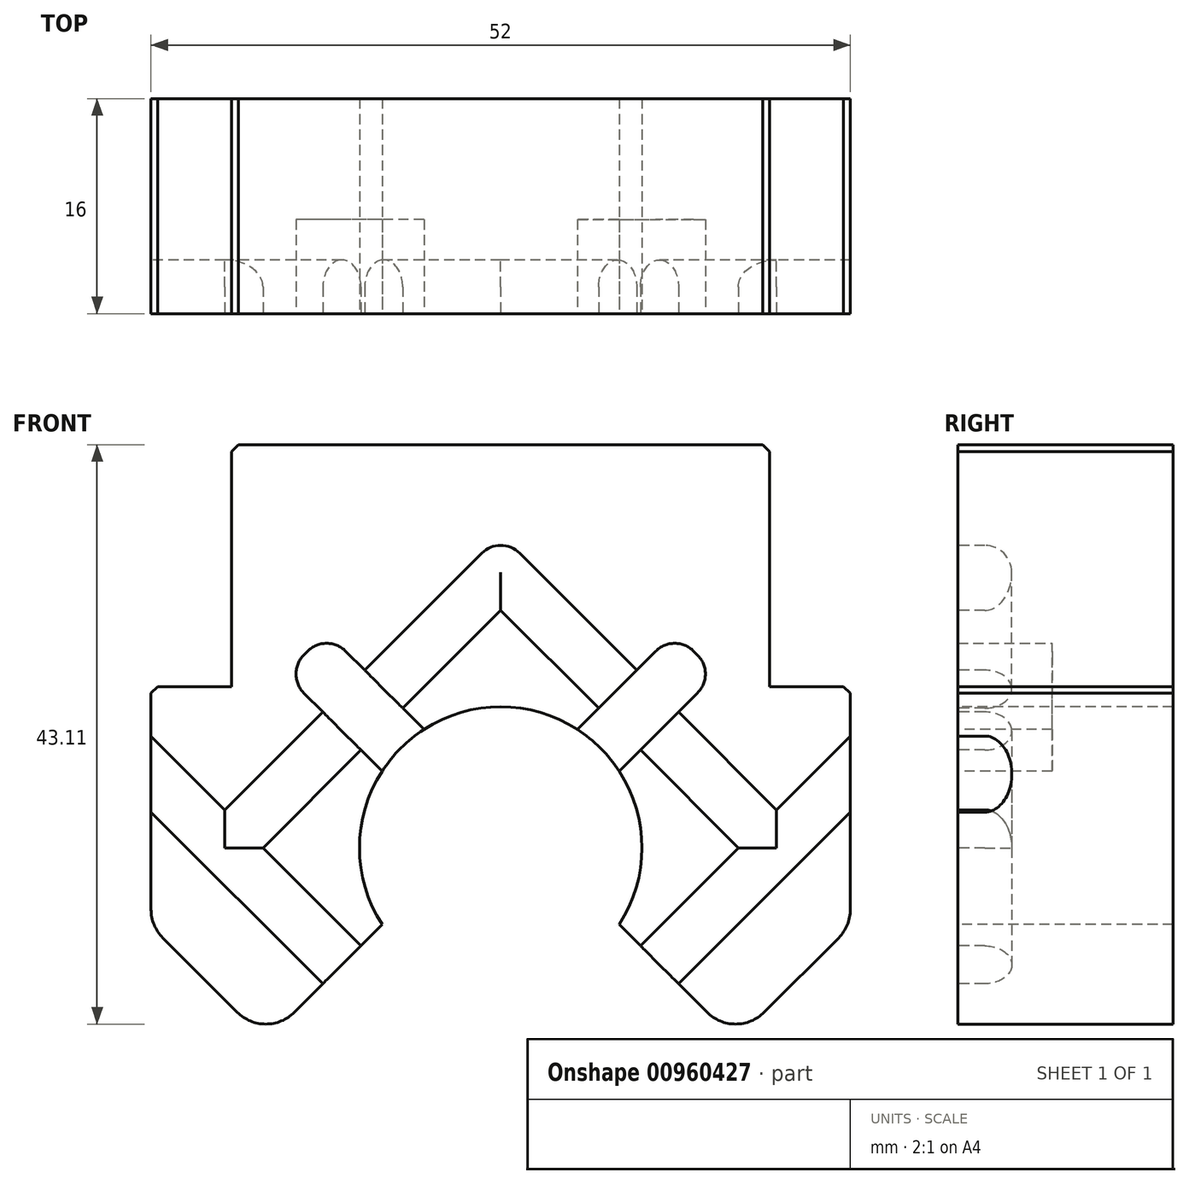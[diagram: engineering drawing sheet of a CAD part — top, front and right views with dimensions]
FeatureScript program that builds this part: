
annotation { "Feature Type Name" : "Feature", "Feature Type Description" : "" }
export const myFeature = defineFeature(function(context is Context, id is Id, definition is map)
    precondition{}
    {
        {
            var Q0;
            Q0=qCreatedBy(makeId("Front.planeOp"),FACE);
            var sketch = newSketch(context, id + "F0", { "sketchPlane" : qUnion([Q0])});
            skLineSegment(sketch, "E0", {"start": v(-23.46, -23.46) * mm, "end": v(26.19, 26.19) * mm, "construction": true});
            skLineSegment(sketch, "E1", {"start": v(-0.37, 20.88) * mm, "end": v(20.54, -0.03) * mm, "construction": true});
            skArc(sketch, "E2", {"start": v(8.82, -5.7) * mm, "mid": v(0, 10.5) * mm, "end": v(-8.82, -5.7) * mm});
            skLineSegment(sketch, "E3", {"start": v(0, -23.09) * mm, "end": v(0, 36.36) * mm, "construction": true});
            skLineSegment(sketch, "E4", {"start": v(-33.15, 0) * mm, "end": v(34.43, 0) * mm, "construction": true});
            skLineSegment(sketch, "E5", {"start": v(0, 30) * mm, "end": v(20, 30) * mm});
            skLineSegment(sketch, "E6", {"start": v(20, 30) * mm, "end": v(20, 12) * mm});
            skLineSegment(sketch, "E7", {"start": v(20, 12) * mm, "end": v(26, 12) * mm});
            skLineSegment(sketch, "E8", {"start": v(26, 12) * mm, "end": v(26, -5.82) * mm});
            skLineSegment(sketch, "E9.MirrorCS", {"start": v(0, 30) * mm, "end": v(-20, 30) * mm});
            skLineSegment(sketch, "E10.MirrorCS", {"start": v(-20, 30) * mm, "end": v(-20, 12) * mm});
            skLineSegment(sketch, "E11.MirrorCS", {"start": v(-20, 12) * mm, "end": v(-26, 12) * mm});
            skLineSegment(sketch, "E12.MirrorCS", {"start": v(-26, 12) * mm, "end": v(-26, -5.82) * mm});
            skLineSegment(sketch, "E13", {"start": v(5.7, 8.82) * mm, "end": v(12.94, 16.05) * mm});
            skLineSegment(sketch, "E14.MirrorCS", {"start": v(8.82, 5.7) * mm, "end": v(16.05, 12.94) * mm});
            skLineSegment(sketch, "E15", {"start": v(12.94, 16.05) * mm, "end": v(16.05, 12.94) * mm});
            skLineSegment(sketch, "E16", {"start": v(0, 17.68) * mm, "end": v(17.68, 0) * mm});
            skLineSegment(sketch, "E17", {"start": v(0, 23.33) * mm, "end": v(20.5, 2.83) * mm});
            skLineSegment(sketch, "E18.MirrorCS", {"start": v(-5.7, 8.82) * mm, "end": v(-12.94, 16.05) * mm});
            skLineSegment(sketch, "E19.MirrorCS", {"start": v(-8.82, 5.7) * mm, "end": v(-16.05, 12.94) * mm});
            skLineSegment(sketch, "E20.MirrorCS", {"start": v(-12.94, 16.05) * mm, "end": v(-16.05, 12.94) * mm});
            skLineSegment(sketch, "E21.MirrorCS", {"start": v(13.22, -10.11) * mm, "end": v(26, 2.67) * mm});
            skLineSegment(sketch, "E22.MirrorCS", {"start": v(10.4, -7.28) * mm, "end": v(17.68, 0) * mm});
            skLineSegment(sketch, "E23.trimOffspring", {"start": v(20.5, 2.83) * mm, "end": v(26, 8.32) * mm});
            skLineSegment(sketch, "E24.MirrorCS", {"start": v(-13.22, -10.11) * mm, "end": v(-26, 2.67) * mm});
            skLineSegment(sketch, "E25.MirrorCS", {"start": v(-10.4, -7.28) * mm, "end": v(-17.68, 0) * mm});
            skLineSegment(sketch, "E26.MirrorCS", {"start": v(0, 17.68) * mm, "end": v(-17.68, 0) * mm});
            skLineSegment(sketch, "E27.MirrorCS", {"start": v(0, 23.33) * mm, "end": v(-20.5, 2.83) * mm});
            skLineSegment(sketch, "E28.MirrorCS", {"start": v(-20.5, 2.83) * mm, "end": v(-26, 8.32) * mm});
            skLineSegment(sketch, "E29", {"start": v(8.82, -5.7) * mm, "end": v(17.47, -14.35) * mm});
            skLineSegment(sketch, "E30", {"start": v(17.47, -14.35) * mm, "end": v(26, -5.82) * mm});
            skLineSegment(sketch, "E31.MirrorCS", {"start": v(-17.47, -14.35) * mm, "end": v(-26, -5.82) * mm});
            skLineSegment(sketch, "E32.MirrorCS", {"start": v(-8.82, -5.7) * mm, "end": v(-17.47, -14.35) * mm});
            skSolve(sketch);
        }
        {
            var Q0;
            {var subQ1=sQuery(id+"F0.wireOp",EDGE,"E2");var subQ7=sQuery(id+"F0.wireOp",EDGE,"E13");var subQ9=makeQuery(id+"F0.imprint","INTERSECT",VERTEX,{"derivedFrom":[subQ1,subQ7]});Q0=makeQuery(id+"F0.imprint","IMPRINT",FACE,{"disambiguationData":[TD([[makeQuery(id+"F0.imprint","IMPRINT",EDGE,{"disambiguationData":[TD([[subQ9,-1.0]])],"derivedFrom":subQ1}),-1.0]])]});}
            var Q1;
            {var subQ0=sQuery(id+"F0.wireOp",EDGE,"E18.MirrorCS");var subQ1=sQuery(id+"F0.wireOp",EDGE,"E2");var subQ2=makeQuery(id+"F0.imprint","INTERSECT",VERTEX,{"derivedFrom":[subQ1,subQ0]});Q1=makeQuery(id+"F0.imprint","IMPRINT",FACE,{"disambiguationData":[TD([[makeQuery(id+"F0.imprint","IMPRINT",EDGE,{"disambiguationData":[TD([[subQ2,-1.0]])],"derivedFrom":subQ1}),-1.0]])]});}
            var Q2;
            {var subQ3=sQuery(id+"F0.wireOp",EDGE,"E25.MirrorCS");Q2=makeQuery(id+"F0.imprint","IMPRINT",FACE,{"disambiguationData":[TD([[makeQuery(id+"F0.imprint","IMPRINT",EDGE,{"derivedFrom":subQ3}),-1.0]])]});}
            var Q3;
            {var subQ0=sQuery(id+"F0.wireOp",EDGE,"E13");var subQ1=sQuery(id+"F0.wireOp",EDGE,"E2");var subQ2=makeQuery(id+"F0.imprint","INTERSECT",VERTEX,{"derivedFrom":[subQ1,subQ0]});Q3=makeQuery(id+"F0.imprint","IMPRINT",FACE,{"disambiguationData":[TD([[makeQuery(id+"F0.imprint","IMPRINT",EDGE,{"disambiguationData":[TD([[subQ2,1.0]])],"derivedFrom":subQ1}),-1.0]])]});}
            var Q4;
            {var subQ7=sQuery(id+"F0.wireOp",EDGE,"E13");var subQ9=sQuery(id+"F0.wireOp",EDGE,"E16");var subQ11=makeQuery(id+"F0.imprint","INTERSECT",VERTEX,{"derivedFrom":[subQ7,subQ9]});Q4=makeQuery(id+"F0.imprint","IMPRINT",FACE,{"disambiguationData":[TD([[makeQuery(id+"F0.imprint","IMPRINT",EDGE,{"disambiguationData":[TD([[subQ11,-1.0]])],"derivedFrom":subQ7}),1.0]])]});}
            var Q5;
            {var subQ0=sQuery(id+"F0.wireOp",EDGE,"E16");var subQ1=sQuery(id+"F0.wireOp",EDGE,"E13");var subQ2=makeQuery(id+"F0.imprint","INTERSECT",VERTEX,{"derivedFrom":[subQ1,subQ0]});Q5=makeQuery(id+"F0.imprint","IMPRINT",FACE,{"disambiguationData":[TD([[makeQuery(id+"F0.imprint","IMPRINT",EDGE,{"disambiguationData":[TD([[subQ2,-1.0]])],"derivedFrom":subQ1}),-1.0]])]});}
            var Q6;
            {var subQ0=sQuery(id+"F0.wireOp",EDGE,"E26.MirrorCS");var subQ1=sQuery(id+"F0.wireOp",EDGE,"E18.MirrorCS");var subQ2=makeQuery(id+"F0.imprint","INTERSECT",VERTEX,{"derivedFrom":[subQ1,subQ0]});Q6=makeQuery(id+"F0.imprint","IMPRINT",FACE,{"disambiguationData":[TD([[makeQuery(id+"F0.imprint","IMPRINT",EDGE,{"disambiguationData":[TD([[subQ2,-1.0]])],"derivedFrom":subQ1}),1.0]])]});}
            var Q7;
            {var subQ0=sQuery(id+"F0.wireOp",EDGE,"E24.MirrorCS");Q7=makeQuery(id+"F0.imprint","IMPRINT",FACE,{"disambiguationData":[TD([[makeQuery(id+"F0.imprint","IMPRINT",EDGE,{"derivedFrom":subQ0}),-1.0]])]});}
            var Q8;
            {var subQ0=sQuery(id+"F0.wireOp",EDGE,"E20.MirrorCS");Q8=makeQuery(id+"F0.imprint","IMPRINT",FACE,{"disambiguationData":[TD([[makeQuery(id+"F0.imprint","IMPRINT",EDGE,{"derivedFrom":subQ0}),1.0]])]});}
            var Q9;
            {var subQ0=sQuery(id+"F0.wireOp",EDGE,"E21.MirrorCS");Q9=makeQuery(id+"F0.imprint","IMPRINT",FACE,{"disambiguationData":[TD([[makeQuery(id+"F0.imprint","IMPRINT",EDGE,{"derivedFrom":subQ0}),1.0]])]});}
            var Q10;
            {var subQ0=sQuery(id+"F0.wireOp",EDGE,"E22.MirrorCS");Q10=makeQuery(id+"F0.imprint","IMPRINT",FACE,{"disambiguationData":[TD([[makeQuery(id+"F0.imprint","IMPRINT",EDGE,{"derivedFrom":subQ0}),1.0]])]});}
            var Q11;
            Q11=makeQuery(id+"F0.imprint","IMPRINT",FACE,{"disambiguationData":[TD([[makeQuery(id+"F0.imprint","IMPRINT",EDGE,{"derivedFrom":sQuery(id+"F0.wireOp",EDGE,"E5")}),-1.0]])]});
            var Q12;
            {var subQ0=sQuery(id+"F0.wireOp",EDGE,"E15");Q12=makeQuery(id+"F0.imprint","IMPRINT",FACE,{"disambiguationData":[TD([[makeQuery(id+"F0.imprint","IMPRINT",EDGE,{"derivedFrom":subQ0}),-1.0]])]});}
            var Q13;
            {var subQ2=sQuery(id+"F0.wireOp",EDGE,"E21.MirrorCS");Q13=makeQuery(id+"F0.imprint","IMPRINT",FACE,{"disambiguationData":[TD([[makeQuery(id+"F0.imprint","IMPRINT",EDGE,{"derivedFrom":subQ2}),-1.0]])]});}
            var Q14;
            {var subQ2=sQuery(id+"F0.wireOp",EDGE,"E24.MirrorCS");Q14=makeQuery(id+"F0.imprint","IMPRINT",FACE,{"disambiguationData":[TD([[makeQuery(id+"F0.imprint","IMPRINT",EDGE,{"derivedFrom":subQ2}),1.0]])]});}
            extrude(context, id + "F1", {"entities" : qUnion([Q0, Q1, Q2, Q3, Q4, Q5, Q6, Q7, Q8, Q9, Q10, Q11, Q12, Q13, Q14]), "oppositeDirection" : true, "depth" : 16 * mm, "offsetDistance" : 25 * mm});
        }
        {
            var Q0;
            {var subQ0=sQuery(id+"F0.wireOp",EDGE,"E15");Q0=makeQuery(id+"F0.imprint","IMPRINT",FACE,{"disambiguationData":[TD([[makeQuery(id+"F0.imprint","IMPRINT",EDGE,{"derivedFrom":subQ0}),-1.0]])]});}
            var Q1;
            {var subQ0=sQuery(id+"F0.wireOp",EDGE,"E16");var subQ1=sQuery(id+"F0.wireOp",EDGE,"E13");var subQ2=makeQuery(id+"F0.imprint","INTERSECT",VERTEX,{"derivedFrom":[subQ1,subQ0]});Q1=makeQuery(id+"F0.imprint","IMPRINT",FACE,{"disambiguationData":[TD([[makeQuery(id+"F0.imprint","IMPRINT",EDGE,{"disambiguationData":[TD([[subQ2,-1.0]])],"derivedFrom":subQ1}),-1.0]])]});}
            var Q2;
            {var subQ0=sQuery(id+"F0.wireOp",EDGE,"E13");var subQ1=sQuery(id+"F0.wireOp",EDGE,"E2");var subQ2=makeQuery(id+"F0.imprint","INTERSECT",VERTEX,{"derivedFrom":[subQ1,subQ0]});Q2=makeQuery(id+"F0.imprint","IMPRINT",FACE,{"disambiguationData":[TD([[makeQuery(id+"F0.imprint","IMPRINT",EDGE,{"disambiguationData":[TD([[subQ2,1.0]])],"derivedFrom":subQ1}),-1.0]])]});}
            var Q3;
            {var subQ0=sQuery(id+"F0.wireOp",EDGE,"E18.MirrorCS");var subQ1=sQuery(id+"F0.wireOp",EDGE,"E2");var subQ2=makeQuery(id+"F0.imprint","INTERSECT",VERTEX,{"derivedFrom":[subQ1,subQ0]});Q3=makeQuery(id+"F0.imprint","IMPRINT",FACE,{"disambiguationData":[TD([[makeQuery(id+"F0.imprint","IMPRINT",EDGE,{"disambiguationData":[TD([[subQ2,-1.0]])],"derivedFrom":subQ1}),-1.0]])]});}
            var Q4;
            {var subQ5=sQuery(id+"F0.wireOp",EDGE,"E20.MirrorCS");Q4=makeQuery(id+"F0.imprint","IMPRINT",FACE,{"disambiguationData":[TD([[makeQuery(id+"F0.imprint","IMPRINT",EDGE,{"derivedFrom":subQ5}),1.0]])]});}
            var Q5;
            {var subQ0=sQuery(id+"F0.wireOp",EDGE,"E26.MirrorCS");var subQ1=sQuery(id+"F0.wireOp",EDGE,"E18.MirrorCS");var subQ2=makeQuery(id+"F0.imprint","INTERSECT",VERTEX,{"derivedFrom":[subQ1,subQ0]});Q5=makeQuery(id+"F0.imprint","IMPRINT",FACE,{"disambiguationData":[TD([[makeQuery(id+"F0.imprint","IMPRINT",EDGE,{"disambiguationData":[TD([[subQ2,-1.0]])],"derivedFrom":subQ1}),1.0]])]});}
            extrude(context, id + "F2", {"entities" : qUnion([Q0, Q1, Q2, Q3, Q4, Q5]), "operationType" : NewBodyOperationType.REMOVE, "oppositeDirection" : true, "depth" : 7 * mm, "offsetDistance" : 25 * mm});
        }
        {
            var Q0;
            {var subQ1=sQuery(id+"F0.wireOp",EDGE,"E16");var subQ8=sQuery(id+"F0.wireOp",EDGE,"E13");var subQ10=makeQuery(id+"F0.imprint","INTERSECT",VERTEX,{"derivedFrom":[subQ8,subQ1]});Q0=makeQuery(id+"F0.imprint","IMPRINT",FACE,{"disambiguationData":[TD([[makeQuery(id+"F0.imprint","IMPRINT",EDGE,{"disambiguationData":[TD([[subQ10,-1.0]])],"derivedFrom":subQ8}),1.0]])]});}
            var Q1;
            {var subQ0=sQuery(id+"F0.wireOp",EDGE,"E21.MirrorCS");Q1=makeQuery(id+"F0.imprint","IMPRINT",FACE,{"disambiguationData":[TD([[makeQuery(id+"F0.imprint","IMPRINT",EDGE,{"derivedFrom":subQ0}),1.0]])]});}
            var Q2;
            {var subQ0=sQuery(id+"F0.wireOp",EDGE,"E24.MirrorCS");Q2=makeQuery(id+"F0.imprint","IMPRINT",FACE,{"disambiguationData":[TD([[makeQuery(id+"F0.imprint","IMPRINT",EDGE,{"derivedFrom":subQ0}),-1.0]])]});}
            extrude(context, id + "F3", {"entities" : qUnion([Q0, Q1, Q2]), "operationType" : NewBodyOperationType.REMOVE, "oppositeDirection" : true, "depth" : 4 * mm, "offsetDistance" : 25 * mm});
        }
        {
            var Q0;
            Q0=makeQuery(id+"F2.boolean.opBoolean","COPY",EDGE,{"derivedFrom":makeQuery(id+"F2.opExtrude","SWEPT_EDGE",EDGE,{"disambiguationData":[OSD([sQuery(id+"F0.wireOp",EDGE,"E19.MirrorCS"),sQuery(id+"F0.wireOp",EDGE,"E20.MirrorCS")])]})});
            var Q1;
            Q1=makeQuery(id+"F2.boolean.opBoolean","COPY",EDGE,{"derivedFrom":makeQuery(id+"F2.opExtrude","SWEPT_EDGE",EDGE,{"disambiguationData":[OSD([sQuery(id+"F0.wireOp",EDGE,"E18.MirrorCS"),sQuery(id+"F0.wireOp",EDGE,"E20.MirrorCS")])]})});
            var Q2;
            Q2=makeQuery(id+"F2.boolean.opBoolean","COPY",EDGE,{"derivedFrom":makeQuery(id+"F2.opExtrude","SWEPT_EDGE",EDGE,{"disambiguationData":[OSD([sQuery(id+"F0.wireOp",EDGE,"E13"),sQuery(id+"F0.wireOp",EDGE,"E15")])]})});
            var Q3;
            Q3=makeQuery(id+"F2.boolean.opBoolean","COPY",EDGE,{"derivedFrom":makeQuery(id+"F2.opExtrude","SWEPT_EDGE",EDGE,{"disambiguationData":[OSD([sQuery(id+"F0.wireOp",EDGE,"E14.MirrorCS"),sQuery(id+"F0.wireOp",EDGE,"E15")])]})});
            var Q4;
            Q4=makeQuery(id+"F3.boolean.opBoolean","COPY",EDGE,{"derivedFrom":makeQuery(id+"F3.opExtrude","SWEPT_EDGE",EDGE,{"disambiguationData":[OSD([sQuery(id+"F0.wireOp",EDGE,"E17"),sQuery(id+"F0.wireOp",EDGE,"E27.MirrorCS")])]})});
            fillet(context, id + "F4", {"entities" : qUnion([Q0, Q1, Q2, Q3, Q4]), "radius" : 2 * mm, "tangentPropagation" : true, "allowEdgeOverflow" : false});
        }
        {
            var Q0;
            {var subQ0=sQuery(id+"F0.wireOp",EDGE,"E16");Q0=makeQuery(id+"F3.boolean.opBoolean","COPY",EDGE,{"derivedFrom":makeQuery(id+"F3.opExtrude","CAP_EDGE",EDGE,{"disambiguationData":[OSD([subQ0]),TDD([makeQuery(id+"F0.imprint","IMPRINT",EDGE,{"disambiguationData":[TD([[makeQuery(id+"F0.imprint","INTERSECT",VERTEX,{"derivedFrom":[subQ0,sQuery(id+"F0.wireOp",EDGE,"5782ae04-5cbb-4565-bf48-bf3dccf2a9680.MirrorCS")]}),-1.0]])],"derivedFrom":subQ0})])],"isStart":false})});}
            var Q1;
            Q1=makeQuery(id+"F3.boolean.opBoolean","COPY",EDGE,{"derivedFrom":makeQuery(id+"F3.opExtrude","CAP_EDGE",EDGE,{"disambiguationData":[OSD([sQuery(id+"F0.wireOp",EDGE,"E21.MirrorCS")])],"isStart":false})});
            var Q2;
            Q2=makeQuery(id+"F3.boolean.opBoolean","COPY",EDGE,{"derivedFrom":makeQuery(id+"F3.opExtrude","CAP_EDGE",EDGE,{"disambiguationData":[OSD([sQuery(id+"F0.wireOp",EDGE,"E22.MirrorCS")])],"isStart":false})});
            var Q3;
            {var subQ0=sQuery(id+"F0.wireOp",EDGE,"E16");Q3=makeQuery(id+"F3.boolean.opBoolean","COPY",EDGE,{"derivedFrom":makeQuery(id+"F3.opExtrude","CAP_EDGE",EDGE,{"disambiguationData":[OSD([subQ0]),TDD([makeQuery(id+"F0.imprint","IMPRINT",EDGE,{"disambiguationData":[TD([[makeQuery(id+"F0.imprint","INTERSECT",VERTEX,{"derivedFrom":[subQ0,sQuery(id+"F0.wireOp",EDGE,"E22.MirrorCS")]}),1.0]])],"derivedFrom":subQ0})])],"isStart":false})});}
            var Q4;
            {var subQ0=sQuery(id+"F0.wireOp",EDGE,"E17");Q4=makeQuery(id+"F3.boolean.opBoolean","COPY",EDGE,{"derivedFrom":makeQuery(id+"F3.opExtrude","CAP_EDGE",EDGE,{"disambiguationData":[OSD([subQ0]),TDD([makeQuery(id+"F0.imprint","IMPRINT",EDGE,{"disambiguationData":[TD([[makeQuery(id+"F0.imprint","INTERSECT",VERTEX,{"derivedFrom":[subQ0,sQuery(id+"F0.wireOp",EDGE,"E23.trimOffspring")]}),1.0]])],"derivedFrom":subQ0})])],"isStart":false})});}
            var Q5;
            {var subQ0=sQuery(id+"F0.wireOp",EDGE,"E17");Q5=makeQuery(id+"F3.boolean.opBoolean","COPY",EDGE,{"derivedFrom":makeQuery(id+"F3.opExtrude","CAP_EDGE",EDGE,{"disambiguationData":[OSD([subQ0]),TDD([makeQuery(id+"F0.imprint","IMPRINT",EDGE,{"disambiguationData":[TD([[makeQuery(id+"F0.imprint","INTERSECT",VERTEX,{"derivedFrom":[subQ0,sQuery(id+"F0.wireOp",EDGE,"E27.MirrorCS")]}),-1.0]])],"derivedFrom":subQ0})])],"isStart":false})});}
            var Q6;
            {var subQ0=sQuery(id+"F0.wireOp",EDGE,"E27.MirrorCS");Q6=makeQuery(id+"F3.boolean.opBoolean","COPY",EDGE,{"derivedFrom":makeQuery(id+"F3.opExtrude","CAP_EDGE",EDGE,{"disambiguationData":[OSD([subQ0]),TDD([makeQuery(id+"F0.imprint","IMPRINT",EDGE,{"disambiguationData":[TD([[makeQuery(id+"F0.imprint","INTERSECT",VERTEX,{"derivedFrom":[subQ0,sQuery(id+"F0.wireOp",EDGE,"E28.MirrorCS")]}),1.0]])],"derivedFrom":subQ0})])],"isStart":false})});}
            var Q7;
            Q7=makeQuery(id+"F3.boolean.opBoolean","COPY",EDGE,{"derivedFrom":makeQuery(id+"F3.opExtrude","CAP_EDGE",EDGE,{"disambiguationData":[OSD([sQuery(id+"F0.wireOp",EDGE,"E28.MirrorCS")])],"isStart":false})});
            var Q8;
            Q8=makeQuery(id+"F3.boolean.opBoolean","COPY",EDGE,{"derivedFrom":makeQuery(id+"F3.opExtrude","CAP_EDGE",EDGE,{"disambiguationData":[OSD([sQuery(id+"F0.wireOp",EDGE,"E25.MirrorCS")])],"isStart":false})});
            var Q9;
            {var subQ0=sQuery(id+"F0.wireOp",EDGE,"E26.MirrorCS");Q9=makeQuery(id+"F3.boolean.opBoolean","COPY",EDGE,{"derivedFrom":makeQuery(id+"F3.opExtrude","CAP_EDGE",EDGE,{"disambiguationData":[OSD([subQ0]),TDD([makeQuery(id+"F0.imprint","IMPRINT",EDGE,{"disambiguationData":[TD([[makeQuery(id+"F0.imprint","INTERSECT",VERTEX,{"derivedFrom":[sQuery(id+"F0.wireOp",EDGE,"E16"),subQ0]}),-1.0]])],"derivedFrom":subQ0})])],"isStart":false})});}
            var Q10;
            {var subQ0=sQuery(id+"F0.wireOp",EDGE,"E26.MirrorCS");Q10=makeQuery(id+"F3.boolean.opBoolean","COPY",EDGE,{"derivedFrom":makeQuery(id+"F3.opExtrude","CAP_EDGE",EDGE,{"disambiguationData":[OSD([subQ0]),TDD([makeQuery(id+"F0.imprint","IMPRINT",EDGE,{"disambiguationData":[TD([[makeQuery(id+"F0.imprint","INTERSECT",VERTEX,{"derivedFrom":[sQuery(id+"F0.wireOp",EDGE,"E25.MirrorCS"),subQ0]}),1.0]])],"derivedFrom":subQ0})])],"isStart":false})});}
            var Q11;
            Q11=makeQuery(id+"F3.boolean.opBoolean","COPY",EDGE,{"derivedFrom":makeQuery(id+"F3.opExtrude","CAP_EDGE",EDGE,{"disambiguationData":[OSD([sQuery(id+"F0.wireOp",EDGE,"E24.MirrorCS")])],"isStart":false})});
            var Q12;
            Q12=makeQuery(id+"F3.boolean.opBoolean","COPY",EDGE,{"derivedFrom":makeQuery(id+"F3.opExtrude","CAP_EDGE",EDGE,{"disambiguationData":[OSD([sQuery(id+"F0.wireOp",EDGE,"E23.trimOffspring")])],"isStart":false})});
            fillet(context, id + "F5", {"entities" : qUnion([Q0, Q1, Q2, Q3, Q4, Q5, Q6, Q7, Q8, Q9, Q10, Q11, Q12]), "radius" : 2 * mm, "tangentPropagation" : true, "allowEdgeOverflow" : false});
        }
        {
            var Q0;
            Q0=makeQuery(id+"F1.opExtrude","SWEPT_EDGE",EDGE,{"disambiguationData":[OSD([sQuery(id+"F0.wireOp",EDGE,"E29"),sQuery(id+"F0.wireOp",EDGE,"E30")])]});
            var Q1;
            Q1=makeQuery(id+"F1.opExtrude","SWEPT_EDGE",EDGE,{"disambiguationData":[OSD([sQuery(id+"F0.wireOp",EDGE,"E8"),sQuery(id+"F0.wireOp",EDGE,"E30")])]});
            var Q2;
            Q2=makeQuery(id+"F1.opExtrude","SWEPT_EDGE",EDGE,{"disambiguationData":[OSD([sQuery(id+"F0.wireOp",EDGE,"E12.MirrorCS"),sQuery(id+"F0.wireOp",EDGE,"E31.MirrorCS")])]});
            var Q3;
            Q3=makeQuery(id+"F1.opExtrude","SWEPT_EDGE",EDGE,{"disambiguationData":[OSD([sQuery(id+"F0.wireOp",EDGE,"E31.MirrorCS"),sQuery(id+"F0.wireOp",EDGE,"E32.MirrorCS")])]});
            fillet(context, id + "F6", {"entities" : qUnion([Q0, Q1, Q2, Q3]), "radius" : 3 * mm, "tangentPropagation" : true, "allowEdgeOverflow" : false});
        }
        {
            var Q0;
            Q0=makeQuery(id+"F1.opExtrude","SWEPT_EDGE",EDGE,{"disambiguationData":[OSD([sQuery(id+"F0.wireOp",EDGE,"E5"),sQuery(id+"F0.wireOp",EDGE,"E6")])]});
            var Q1;
            Q1=makeQuery(id+"F1.opExtrude","SWEPT_EDGE",EDGE,{"disambiguationData":[OSD([sQuery(id+"F0.wireOp",EDGE,"E7"),sQuery(id+"F0.wireOp",EDGE,"E8")])]});
            var Q2;
            Q2=makeQuery(id+"F1.opExtrude","SWEPT_EDGE",EDGE,{"disambiguationData":[OSD([sQuery(id+"F0.wireOp",EDGE,"E9.MirrorCS"),sQuery(id+"F0.wireOp",EDGE,"E10.MirrorCS")])]});
            var Q3;
            Q3=makeQuery(id+"F1.opExtrude","SWEPT_EDGE",EDGE,{"disambiguationData":[OSD([sQuery(id+"F0.wireOp",EDGE,"E11.MirrorCS"),sQuery(id+"F0.wireOp",EDGE,"E12.MirrorCS")])]});
            chamfer(context, id + "F7", {"entities" : qUnion([Q0, Q1, Q2, Q3]), "width" : 0.5 * mm, "tangentPropagation" : true});
        }
    });
